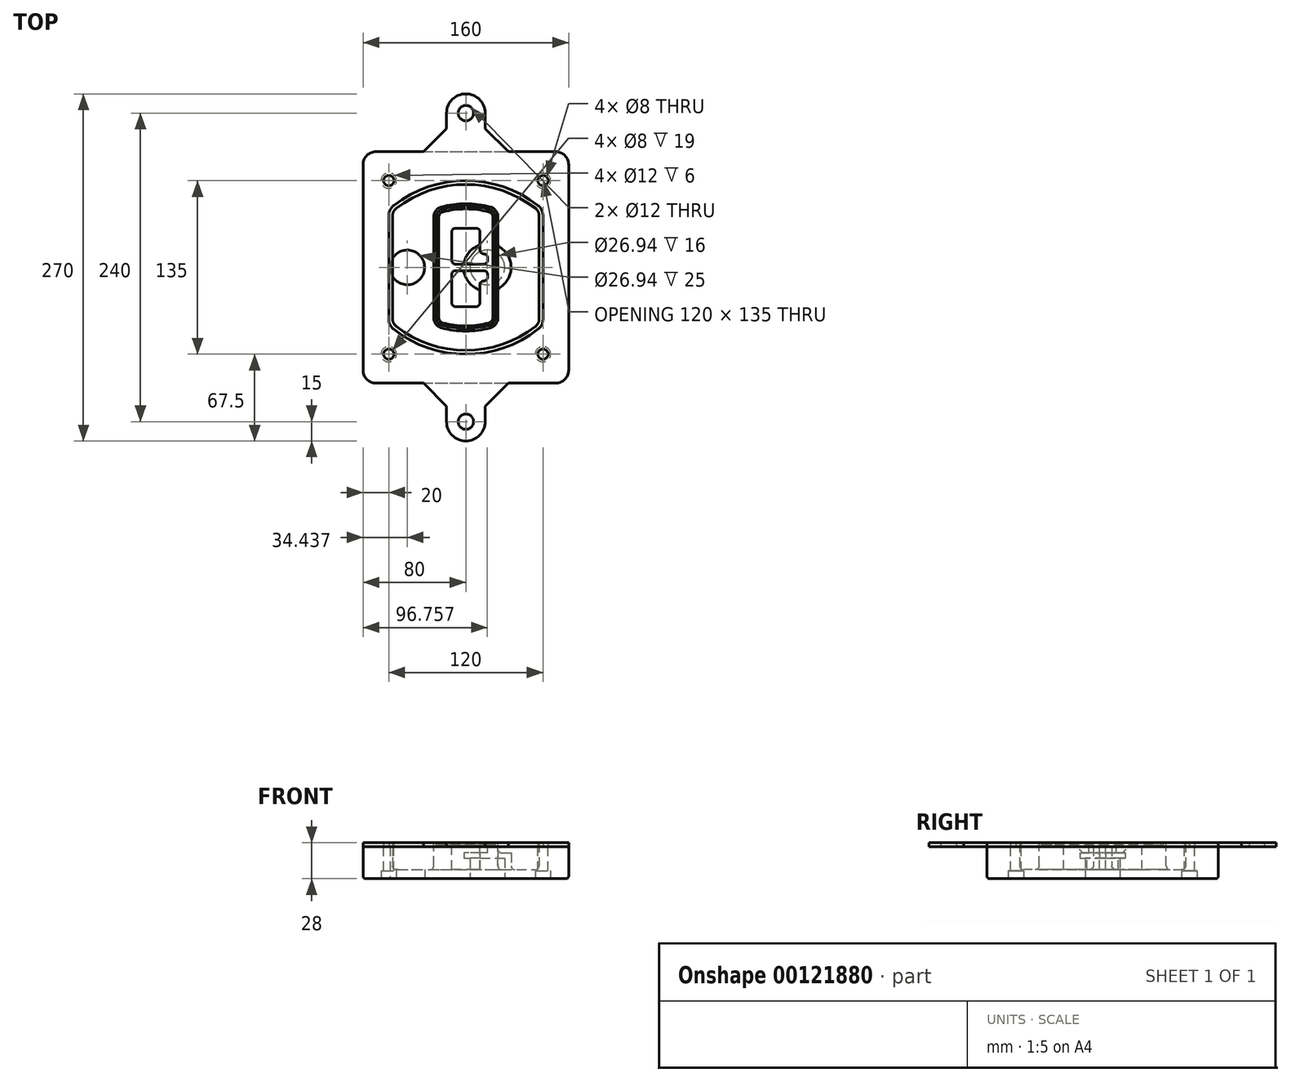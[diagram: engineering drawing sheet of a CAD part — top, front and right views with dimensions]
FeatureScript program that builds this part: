
annotation { "Feature Type Name" : "Feature", "Feature Type Description" : "" }
export const myFeature = defineFeature(function(context is Context, id is Id, definition is map)
    precondition{}
    {
        {
            var Q0;
            Q0=qCreatedBy(makeId("Top.planeOp"),FACE);
            var sketch = newSketch(context, id + "F0", { "sketchPlane" : qUnion([Q0])});
            skPoint(sketch, "E0.rect.middle", {"position": v(0, 0) * mm});
            skLineSegment(sketch, "E1.bottom", {"start": v(-70, -90) * mm, "end": v(70, -90) * mm});
            skLineSegment(sketch, "E1.top", {"start": v(-70, 90) * mm, "end": v(70, 90) * mm});
            skLineSegment(sketch, "E1.left", {"start": v(-80, -80) * mm, "end": v(-80, 80) * mm});
            skLineSegment(sketch, "E1.right", {"start": v(80, -80) * mm, "end": v(80, 80) * mm});
            skLineSegment(sketch, "E2", {"start": v(-80, 90) * mm, "end": v(80, -90) * mm, "construction": true});
            skLineSegment(sketch, "E3", {"start": v(80, 90) * mm, "end": v(-80, -90) * mm, "construction": true});
            skCircle(sketch, "E4", {"center": v(-60, 67.5) * mm, "radius": 4 * mm});
            skCircle(sketch, "E5", {"center": v(60, 67.5) * mm, "radius": 4 * mm});
            skCircle(sketch, "E6", {"center": v(60, -67.5) * mm, "radius": 4 * mm});
            skCircle(sketch, "E7", {"center": v(-60, -67.5) * mm, "radius": 4 * mm});
            skLineSegment(sketch, "E8", {"start": v(-60, 67.5) * mm, "end": v(60, 67.5) * mm, "construction": true});
            skLineSegment(sketch, "E9", {"start": v(60, 67.5) * mm, "end": v(60, -67.5) * mm, "construction": true});
            skLineSegment(sketch, "E10", {"start": v(60, -67.5) * mm, "end": v(-60, -67.5) * mm, "construction": true});
            skLineSegment(sketch, "E11", {"start": v(-60, -67.5) * mm, "end": v(-60, 67.5) * mm, "construction": true});
            skLineSegment(sketch, "E12", {"start": v(-60, 40.3) * mm, "end": v(-60, -40.3) * mm});
            skLineSegment(sketch, "E13", {"start": v(60, 40.3) * mm, "end": v(60, -40.3) * mm});
            skArc(sketch, "E14", {"start": v(56.15, 48.18) * mm, "mid": v(0, 67.5) * mm, "end": v(-56.15, 48.18) * mm});
            skArc(sketch, "E15", {"start": v(-56.15, -48.18) * mm, "mid": v(0, -67.5) * mm, "end": v(56.15, -48.18) * mm});
            skLineSegment(sketch, "E16", {"start": v(-60, 0) * mm, "end": v(60, 0) * mm, "construction": true});
            skPoint(sketch, "E17.visualSharp", {"position": v(-60, -45) * mm});
            skArc(sketch, "E17.filletArc", {"start": v(-60, -40.3) * mm, "mid": v(-58.99, -44.68) * mm, "end": v(-56.15, -48.18) * mm});
            skPoint(sketch, "E18.visualSharp", {"position": v(-60, 45) * mm});
            skArc(sketch, "E18.filletArc", {"start": v(-56.15, 48.18) * mm, "mid": v(-58.99, 44.68) * mm, "end": v(-60, 40.3) * mm});
            skPoint(sketch, "E19.visualSharp", {"position": v(60, 45) * mm});
            skArc(sketch, "E19.filletArc", {"start": v(60, 40.3) * mm, "mid": v(58.99, 44.68) * mm, "end": v(56.15, 48.18) * mm});
            skPoint(sketch, "E20.visualSharp", {"position": v(60, -45) * mm});
            skArc(sketch, "E20.filletArc", {"start": v(56.15, -48.18) * mm, "mid": v(58.99, -44.68) * mm, "end": v(60, -40.3) * mm});
            skPoint(sketch, "E21.visualSharp", {"position": v(-80, 90) * mm});
            skArc(sketch, "E21.filletArc", {"start": v(-70, 90) * mm, "mid": v(-77.07, 87.07) * mm, "end": v(-80, 80) * mm});
            skPoint(sketch, "E22.visualSharp", {"position": v(80, 90) * mm});
            skArc(sketch, "E22.filletArc", {"start": v(80, 80) * mm, "mid": v(77.07, 87.07) * mm, "end": v(70, 90) * mm});
            skPoint(sketch, "E23.visualSharp", {"position": v(80, -90) * mm});
            skArc(sketch, "E23.filletArc", {"start": v(70, -90) * mm, "mid": v(77.07, -87.07) * mm, "end": v(80, -80) * mm});
            skPoint(sketch, "E24.visualSharp", {"position": v(-80, -90) * mm});
            skArc(sketch, "E24.filletArc", {"start": v(-80, -80) * mm, "mid": v(-77.07, -87.07) * mm, "end": v(-70, -90) * mm});
            skArc(sketch, "E25.0", {"start": v(57, 40.3) * mm, "mid": v(56.3, 43.36) * mm, "end": v(54.3, 45.81) * mm});
            skLineSegment(sketch, "E25.1", {"start": v(57, 40.3) * mm, "end": v(57, -40.3) * mm});
            skArc(sketch, "E25.2", {"start": v(54.3, -45.81) * mm, "mid": v(56.3, -43.36) * mm, "end": v(57, -40.3) * mm});
            skArc(sketch, "E25.3", {"start": v(-54.3, -45.81) * mm, "mid": v(0, -64.5) * mm, "end": v(54.3, -45.81) * mm});
            skArc(sketch, "E25.4", {"start": v(-57, -40.3) * mm, "mid": v(-56.3, -43.36) * mm, "end": v(-54.3, -45.81) * mm});
            skArc(sketch, "E25.5", {"start": v(54.3, 45.81) * mm, "mid": v(0, 64.5) * mm, "end": v(-54.3, 45.81) * mm});
            skLineSegment(sketch, "E25.6", {"start": v(-57, 40.3) * mm, "end": v(-57, -40.3) * mm});
            skArc(sketch, "E25.7", {"start": v(-54.3, 45.81) * mm, "mid": v(-56.3, 43.36) * mm, "end": v(-57, 40.3) * mm});
            skArc(sketch, "E26.0", {"start": v(-58.62, 51.33) * mm, "mid": v(-62.58, 46.43) * mm, "end": v(-64, 40.3) * mm});
            skArc(sketch, "E26.1", {"start": v(58.62, 51.33) * mm, "mid": v(0, 71.5) * mm, "end": v(-58.62, 51.33) * mm});
            skArc(sketch, "E26.2", {"start": v(64, 40.3) * mm, "mid": v(62.58, 46.43) * mm, "end": v(58.62, 51.33) * mm});
            skLineSegment(sketch, "E26.3", {"start": v(64, 40.3) * mm, "end": v(64, -40.3) * mm});
            skArc(sketch, "E26.4", {"start": v(58.62, -51.33) * mm, "mid": v(62.58, -46.43) * mm, "end": v(64, -40.3) * mm});
            skLineSegment(sketch, "E26.5", {"start": v(-64, 40.3) * mm, "end": v(-64, -40.3) * mm});
            skArc(sketch, "E26.6", {"start": v(-58.62, -51.33) * mm, "mid": v(0, -71.5) * mm, "end": v(58.62, -51.33) * mm});
            skArc(sketch, "E26.7", {"start": v(-64, -40.3) * mm, "mid": v(-62.58, -46.43) * mm, "end": v(-58.62, -51.33) * mm});
            skSolve(sketch);
        }
        {
            var Q0;
            Q0=makeQuery(id+"F0.imprint","IMPRINT",FACE,{"disambiguationData":[TD([[makeQuery(id+"F0.imprint","IMPRINT",EDGE,{"derivedFrom":sQuery(id+"F0.wireOp",EDGE,"E1.bottom")}),1.0]])]});
            var Q1;
            Q1=makeQuery(id+"F0.imprint","IMPRINT",FACE,{"disambiguationData":[TD([[makeQuery(id+"F0.imprint","IMPRINT",EDGE,{"derivedFrom":sQuery(id+"F0.wireOp",EDGE,"E12")}),1.0]])]});
            var Q2;
            Q2=makeQuery(id+"F0.imprint","IMPRINT",FACE,{"disambiguationData":[TD([[makeQuery(id+"F0.imprint","IMPRINT",EDGE,{"derivedFrom":sQuery(id+"F0.wireOp",EDGE,"E25.0")}),1.0]])]});
            var Q3;
            Q3=makeQuery(id+"F0.imprint","IMPRINT",FACE,{"disambiguationData":[TD([[makeQuery(id+"F0.imprint","IMPRINT",EDGE,{"derivedFrom":sQuery(id+"F0.wireOp",EDGE,"E12")}),-1.0]])]});
            extrude(context, id + "F1", {"entities" : qUnion([Q0, Q1, Q2, Q3]), "oppositeDirection" : true, "depth" : 25 * mm});
        }
        {
            var Q0;
            Q0=makeQuery(id+"F0.imprint","IMPRINT",FACE,{"disambiguationData":[TD([[makeQuery(id+"F0.imprint","IMPRINT",EDGE,{"derivedFrom":sQuery(id+"F0.wireOp",EDGE,"E12")}),1.0]])]});
            extrude(context, id + "F2", {"entities" : qUnion([Q0]), "operationType" : NewBodyOperationType.ADD, "depth" : 3 * mm});
        }
        {
            var Q0;
            Q0=makeQuery(id+"F0.imprint","IMPRINT",FACE,{"disambiguationData":[TD([[makeQuery(id+"F0.imprint","IMPRINT",EDGE,{"derivedFrom":sQuery(id+"F0.wireOp",EDGE,"E25.0")}),1.0]])]});
            extrude(context, id + "F3", {"entities" : qUnion([Q0]), "operationType" : NewBodyOperationType.REMOVE, "oppositeDirection" : true, "depth" : 18 * mm});
        }
        {
            var Q0;
            Q0=makeQuery(id+"F2.opExtrude","CAP_FACE",FACE,{"disambiguationData":[OSD([sQuery(id+"F0.wireOp",EDGE,"E12"),sQuery(id+"F0.wireOp",EDGE,"E13"),sQuery(id+"F0.wireOp",EDGE,"E14"),sQuery(id+"F0.wireOp",EDGE,"E15"),sQuery(id+"F0.wireOp",EDGE,"E17.filletArc"),sQuery(id+"F0.wireOp",EDGE,"E18.filletArc"),sQuery(id+"F0.wireOp",EDGE,"E19.filletArc"),sQuery(id+"F0.wireOp",EDGE,"E20.filletArc"),sQuery(id+"F0.wireOp",EDGE,"E25.0"),sQuery(id+"F0.wireOp",EDGE,"E25.1"),sQuery(id+"F0.wireOp",EDGE,"E25.2"),sQuery(id+"F0.wireOp",EDGE,"E25.3"),sQuery(id+"F0.wireOp",EDGE,"E25.4"),sQuery(id+"F0.wireOp",EDGE,"E25.5"),sQuery(id+"F0.wireOp",EDGE,"E25.6"),sQuery(id+"F0.wireOp",EDGE,"E25.7")])],"isStart":false});
            var sketch = newSketch(context, id + "F4", { "sketchPlane" : qUnion([Q0])});
            skArc(sketch, "E27.0", {"start": v(-19.08, -46.97) * mm, "mid": v(0, -49.5) * mm, "end": v(19.08, -46.97) * mm});
            skArc(sketch, "E28.0", {"start": v(19.08, 46.97) * mm, "mid": v(0, 49.5) * mm, "end": v(-19.08, 46.97) * mm});
            skLineSegment(sketch, "E29", {"start": v(-25, 39.25) * mm, "end": v(-25, -39.25) * mm});
            skLineSegment(sketch, "E30", {"start": v(25, 39.25) * mm, "end": v(25, -39.25) * mm});
            skLineSegment(sketch, "E31", {"start": v(-25, 45.1) * mm, "end": v(25, 45.1) * mm, "construction": true});
            skLineSegment(sketch, "E32", {"start": v(-25, -45.1) * mm, "end": v(25, -45.1) * mm, "construction": true});
            skPoint(sketch, "E33.visualSharp", {"position": v(-25, 45.1) * mm});
            skArc(sketch, "E33.filletArc", {"start": v(-19.08, 46.97) * mm, "mid": v(-23.35, 44.11) * mm, "end": v(-25, 39.25) * mm});
            skPoint(sketch, "E34.visualSharp", {"position": v(25, 45.1) * mm});
            skArc(sketch, "E34.filletArc", {"start": v(25, 39.25) * mm, "mid": v(23.35, 44.11) * mm, "end": v(19.08, 46.97) * mm});
            skPoint(sketch, "E35.visualSharp", {"position": v(25, -45.1) * mm});
            skArc(sketch, "E35.filletArc", {"start": v(19.08, -46.97) * mm, "mid": v(23.35, -44.11) * mm, "end": v(25, -39.25) * mm});
            skPoint(sketch, "E36.visualSharp", {"position": v(-25, -45.1) * mm});
            skArc(sketch, "E36.filletArc", {"start": v(-25, -39.25) * mm, "mid": v(-23.35, -44.11) * mm, "end": v(-19.08, -46.97) * mm});
            skArc(sketch, "E37.0", {"start": v(54.3, 45.81) * mm, "mid": v(0, 64.5) * mm, "end": v(-54.3, 45.81) * mm});
            skArc(sketch, "E37.1", {"start": v(-54.3, 45.81) * mm, "mid": v(-56.3, 43.36) * mm, "end": v(-57, 40.3) * mm});
            skLineSegment(sketch, "E37.2", {"start": v(-57, 40.3) * mm, "end": v(-57, -40.3) * mm});
            skArc(sketch, "E37.3", {"start": v(-57, -40.3) * mm, "mid": v(-56.3, -43.36) * mm, "end": v(-54.3, -45.81) * mm});
            skArc(sketch, "E37.4", {"start": v(-54.3, -45.81) * mm, "mid": v(0, -64.5) * mm, "end": v(54.3, -45.81) * mm});
            skArc(sketch, "E37.5", {"start": v(54.3, -45.81) * mm, "mid": v(56.3, -43.36) * mm, "end": v(57, -40.3) * mm});
            skLineSegment(sketch, "E37.6", {"start": v(57, 40.3) * mm, "end": v(57, -40.3) * mm});
            skArc(sketch, "E37.7", {"start": v(57, 40.3) * mm, "mid": v(56.3, 43.36) * mm, "end": v(54.3, 45.81) * mm});
            skLineSegment(sketch, "E38.0", {"start": v(23, 39.25) * mm, "end": v(23, -39.25) * mm});
            skArc(sketch, "E38.1", {"start": v(18.56, -45.04) * mm, "mid": v(21.76, -42.9) * mm, "end": v(23, -39.25) * mm});
            skArc(sketch, "E38.2", {"start": v(-18.56, -45.04) * mm, "mid": v(0, -47.5) * mm, "end": v(18.56, -45.04) * mm});
            skArc(sketch, "E38.3", {"start": v(-23, -39.25) * mm, "mid": v(-21.76, -42.9) * mm, "end": v(-18.56, -45.04) * mm});
            skLineSegment(sketch, "E38.4", {"start": v(-23, 39.25) * mm, "end": v(-23, -39.25) * mm});
            skArc(sketch, "E38.5", {"start": v(23, 39.25) * mm, "mid": v(21.76, 42.9) * mm, "end": v(18.56, 45.04) * mm});
            skArc(sketch, "E38.6", {"start": v(-18.56, 45.04) * mm, "mid": v(-21.76, 42.9) * mm, "end": v(-23, 39.25) * mm});
            skArc(sketch, "E38.7", {"start": v(18.56, 45.04) * mm, "mid": v(0, 47.5) * mm, "end": v(-18.56, 45.04) * mm});
            skArc(sketch, "E39.0", {"start": v(21, 39.25) * mm, "mid": v(20.18, 41.68) * mm, "end": v(18.04, 43.1) * mm});
            skLineSegment(sketch, "E39.1", {"start": v(21, 39.25) * mm, "end": v(21, -39.25) * mm});
            skArc(sketch, "E39.2", {"start": v(18.04, -43.1) * mm, "mid": v(20.18, -41.68) * mm, "end": v(21, -39.25) * mm});
            skArc(sketch, "E39.3", {"start": v(-18.04, -43.1) * mm, "mid": v(0, -45.5) * mm, "end": v(18.04, -43.1) * mm});
            skArc(sketch, "E39.4", {"start": v(-21, -39.25) * mm, "mid": v(-20.18, -41.68) * mm, "end": v(-18.04, -43.1) * mm});
            skArc(sketch, "E39.5", {"start": v(18.04, 43.1) * mm, "mid": v(0, 45.5) * mm, "end": v(-18.04, 43.1) * mm});
            skLineSegment(sketch, "E39.6", {"start": v(-21, 39.25) * mm, "end": v(-21, -39.25) * mm});
            skArc(sketch, "E39.7", {"start": v(-18.04, 43.1) * mm, "mid": v(-20.18, 41.68) * mm, "end": v(-21, 39.25) * mm});
            skLineSegment(sketch, "E40", {"start": v(-25, 0) * mm, "end": v(25, 0) * mm, "construction": true});
            skLineSegment(sketch, "E41", {"start": v(-11, 5.5) * mm, "end": v(-11, 27.5) * mm});
            skLineSegment(sketch, "E42", {"start": v(-8, 30.5) * mm, "end": v(8, 30.5) * mm});
            skLineSegment(sketch, "E43", {"start": v(11, 27.5) * mm, "end": v(11, 13.5) * mm});
            skLineSegment(sketch, "E44", {"start": v(14, 10.5) * mm, "end": v(14, 10.5) * mm});
            skLineSegment(sketch, "E45", {"start": v(17, 7.5) * mm, "end": v(17, 5.5) * mm});
            skLineSegment(sketch, "E46", {"start": v(14, 2.5) * mm, "end": v(-8, 2.5) * mm});
            skPoint(sketch, "E47.visualSharp", {"position": v(-11, 30.5) * mm});
            skArc(sketch, "E47.filletArc", {"start": v(-8, 30.5) * mm, "mid": v(-10.12, 29.62) * mm, "end": v(-11, 27.5) * mm});
            skPoint(sketch, "E48.visualSharp", {"position": v(11, 30.5) * mm});
            skArc(sketch, "E48.filletArc", {"start": v(11, 27.5) * mm, "mid": v(10.12, 29.62) * mm, "end": v(8, 30.5) * mm});
            skPoint(sketch, "E49.visualSharp", {"position": v(11, 10.5) * mm});
            skArc(sketch, "E49.filletArc", {"start": v(11, 13.5) * mm, "mid": v(11.88, 11.38) * mm, "end": v(14, 10.5) * mm});
            skPoint(sketch, "E50.visualSharp", {"position": v(17, 10.5) * mm});
            skArc(sketch, "E50.filletArc", {"start": v(17, 7.5) * mm, "mid": v(16.12, 9.62) * mm, "end": v(14, 10.5) * mm});
            skPoint(sketch, "E51.visualSharp", {"position": v(17, 2.5) * mm});
            skArc(sketch, "E51.filletArc", {"start": v(14, 2.5) * mm, "mid": v(16.12, 3.38) * mm, "end": v(17, 5.5) * mm});
            skPoint(sketch, "E52.visualSharp", {"position": v(-11, 2.5) * mm});
            skArc(sketch, "E52.filletArc", {"start": v(-11, 5.5) * mm, "mid": v(-10.12, 3.38) * mm, "end": v(-8, 2.5) * mm});
            skLineSegment(sketch, "E53.0.MirrorCS", {"start": v(14, -2.5) * mm, "end": v(-8, -2.5) * mm});
            skArc(sketch, "E54.0.MirrorCS", {"start": v(-11, -5.5) * mm, "mid": v(-10.12, -3.38) * mm, "end": v(-8, -2.5) * mm});
            skLineSegment(sketch, "E55.0.MirrorCS", {"start": v(-11, -5.5) * mm, "end": v(-11, -27.5) * mm});
            skArc(sketch, "E56.0.MirrorCS", {"start": v(-8, -30.5) * mm, "mid": v(-10.12, -29.62) * mm, "end": v(-11, -27.5) * mm});
            skLineSegment(sketch, "E57.0.MirrorCS", {"start": v(-8, -30.5) * mm, "end": v(8, -30.5) * mm});
            skArc(sketch, "E58.0.MirrorCS", {"start": v(11, -27.5) * mm, "mid": v(10.12, -29.62) * mm, "end": v(8, -30.5) * mm});
            skLineSegment(sketch, "E59.0.MirrorCS", {"start": v(11, -27.5) * mm, "end": v(11, -13.5) * mm});
            skArc(sketch, "E60.0.MirrorCS", {"start": v(11, -13.5) * mm, "mid": v(11.88, -11.38) * mm, "end": v(14, -10.5) * mm});
            skArc(sketch, "E61.0.MirrorCS", {"start": v(17, -7.5) * mm, "mid": v(16.12, -9.62) * mm, "end": v(14, -10.5) * mm});
            skLineSegment(sketch, "E62.0.MirrorCS", {"start": v(17, -7.5) * mm, "end": v(17, -5.5) * mm});
            skArc(sketch, "E63.0.MirrorCS", {"start": v(14, -2.5) * mm, "mid": v(16.12, -3.38) * mm, "end": v(17, -5.5) * mm});
            skSolve(sketch);
        }
        {
            var Q0;
            Q0=makeQuery(id+"F4.imprint","IMPRINT",FACE,{"disambiguationData":[TD([[makeQuery(id+"F4.imprint","IMPRINT",EDGE,{"derivedFrom":sQuery(id+"F4.wireOp",EDGE,"E27.0")}),1.0]])]});
            var Q1;
            Q1=makeQuery(id+"F4.imprint","IMPRINT",FACE,{"disambiguationData":[TD([[makeQuery(id+"F4.imprint","IMPRINT",EDGE,{"derivedFrom":sQuery(id+"F4.wireOp",EDGE,"E38.0")}),-1.0]])]});
            var Q2;
            Q2=makeQuery(id+"F4.imprint","IMPRINT",FACE,{"disambiguationData":[TD([[makeQuery(id+"F4.imprint","IMPRINT",EDGE,{"derivedFrom":sQuery(id+"F4.wireOp",EDGE,"E39.0")}),1.0]])]});
            extrude(context, id + "F5", {"entities" : qUnion([Q0, Q1, Q2]), "operationType" : NewBodyOperationType.ADD, "endBound" : BoundingType.UP_TO_NEXT, "oppositeDirection" : true, "depth" : 25 * mm});
        }
        {
            var Q0;
            Q0=makeQuery(id+"F4.imprint","IMPRINT",FACE,{"disambiguationData":[TD([[makeQuery(id+"F4.imprint","IMPRINT",EDGE,{"derivedFrom":sQuery(id+"F4.wireOp",EDGE,"E38.0")}),-1.0]])]});
            extrude(context, id + "F6", {"entities" : qUnion([Q0]), "operationType" : NewBodyOperationType.REMOVE, "oppositeDirection" : true, "depth" : 2 * mm});
        }
        {
            var Q0;
            Q0=makeQuery(id+"F1.opExtrude","CAP_FACE",FACE,{"disambiguationData":[OSD([sQuery(id+"F0.wireOp",EDGE,"E1.bottom"),sQuery(id+"F0.wireOp",EDGE,"E1.top"),sQuery(id+"F0.wireOp",EDGE,"E1.left"),sQuery(id+"F0.wireOp",EDGE,"E1.right"),sQuery(id+"F0.wireOp",EDGE,"E4"),sQuery(id+"F0.wireOp",EDGE,"E5"),sQuery(id+"F0.wireOp",EDGE,"E6"),sQuery(id+"F0.wireOp",EDGE,"E7"),sQuery(id+"F0.wireOp",EDGE,"E21.filletArc"),sQuery(id+"F0.wireOp",EDGE,"E22.filletArc"),sQuery(id+"F0.wireOp",EDGE,"E23.filletArc"),sQuery(id+"F0.wireOp",EDGE,"E24.filletArc")])],"isStart":false});
            var sketch = newSketch(context, id + "F7", { "sketchPlane" : qUnion([Q0])});
            skCircle(sketch, "E64", {"center": v(16.76, 0) * mm, "radius": 13.47 * mm});
            skCircle(sketch, "E65", {"center": v(-45.56, 0) * mm, "radius": 13.47 * mm});
            skLineSegment(sketch, "E66", {"start": v(80, 0) * mm, "end": v(-80, 0) * mm});
            skCircle(sketch, "E67", {"center": v(16.76, 0) * mm, "radius": 18.47 * mm});
            skCircle(sketch, "E68", {"center": v(60, -67.5) * mm, "radius": 6 * mm});
            skCircle(sketch, "E69", {"center": v(-60, -67.5) * mm, "radius": 6 * mm});
            skCircle(sketch, "E70", {"center": v(-60, 67.5) * mm, "radius": 6 * mm});
            skCircle(sketch, "E71", {"center": v(60, 67.5) * mm, "radius": 6 * mm});
            skSolve(sketch);
        }
        {
            var Q0;
            {var subQ1=sQuery(id+"F7.wireOp",EDGE,"E66");var subQ4=sQuery(id+"F7.wireOp",EDGE,"E64");var subQ6=makeQuery(id+"F7.imprint","INTERSECT",VERTEX,{"disambiguationData":[OD(0.0)],"derivedFrom":[subQ4,subQ1]});Q0=makeQuery(id+"F7.imprint","IMPRINT",FACE,{"disambiguationData":[TD([[makeQuery(id+"F7.imprint","IMPRINT",EDGE,{"disambiguationData":[TD([[subQ6,-1.0]])],"derivedFrom":subQ4}),-1.0]])]});}
            var Q1;
            {var subQ0=sQuery(id+"F7.wireOp",EDGE,"E66");var subQ1=sQuery(id+"F7.wireOp",EDGE,"E64");var subQ3=makeQuery(id+"F7.imprint","INTERSECT",VERTEX,{"disambiguationData":[OD(0.0)],"derivedFrom":[subQ1,subQ0]});Q1=makeQuery(id+"F7.imprint","IMPRINT",FACE,{"disambiguationData":[TD([[makeQuery(id+"F7.imprint","IMPRINT",EDGE,{"disambiguationData":[TD([[subQ3,-1.0]])],"derivedFrom":subQ1}),1.0]])]});}
            var Q2;
            {var subQ0=sQuery(id+"F7.wireOp",EDGE,"E66");var subQ1=sQuery(id+"F7.wireOp",EDGE,"E64");var subQ3=makeQuery(id+"F7.imprint","INTERSECT",VERTEX,{"disambiguationData":[OD(0.0)],"derivedFrom":[subQ1,subQ0]});Q2=makeQuery(id+"F7.imprint","IMPRINT",FACE,{"disambiguationData":[TD([[makeQuery(id+"F7.imprint","IMPRINT",EDGE,{"disambiguationData":[TD([[subQ3,1.0]])],"derivedFrom":subQ1}),1.0]])]});}
            var Q3;
            {var subQ1=sQuery(id+"F7.wireOp",EDGE,"E66");var subQ4=sQuery(id+"F7.wireOp",EDGE,"E64");var subQ6=makeQuery(id+"F7.imprint","INTERSECT",VERTEX,{"disambiguationData":[OD(0.0)],"derivedFrom":[subQ4,subQ1]});Q3=makeQuery(id+"F7.imprint","IMPRINT",FACE,{"disambiguationData":[TD([[makeQuery(id+"F7.imprint","IMPRINT",EDGE,{"disambiguationData":[TD([[subQ6,1.0]])],"derivedFrom":subQ4}),-1.0]])]});}
            extrude(context, id + "F8", {"entities" : qUnion([Q0, Q1, Q2, Q3]), "operationType" : NewBodyOperationType.ADD, "oppositeDirection" : true, "depth" : 20 * mm});
        }
        {
            var Q0;
            {var subQ0=sQuery(id+"F7.wireOp",EDGE,"E66");var subQ1=sQuery(id+"F7.wireOp",EDGE,"E64");var subQ3=makeQuery(id+"F7.imprint","INTERSECT",VERTEX,{"disambiguationData":[OD(0.0)],"derivedFrom":[subQ1,subQ0]});Q0=makeQuery(id+"F7.imprint","IMPRINT",FACE,{"disambiguationData":[TD([[makeQuery(id+"F7.imprint","IMPRINT",EDGE,{"disambiguationData":[TD([[subQ3,-1.0]])],"derivedFrom":subQ1}),1.0]])]});}
            var Q1;
            {var subQ0=sQuery(id+"F7.wireOp",EDGE,"E66");var subQ1=sQuery(id+"F7.wireOp",EDGE,"E64");var subQ3=makeQuery(id+"F7.imprint","INTERSECT",VERTEX,{"disambiguationData":[OD(0.0)],"derivedFrom":[subQ1,subQ0]});Q1=makeQuery(id+"F7.imprint","IMPRINT",FACE,{"disambiguationData":[TD([[makeQuery(id+"F7.imprint","IMPRINT",EDGE,{"disambiguationData":[TD([[subQ3,1.0]])],"derivedFrom":subQ1}),1.0]])]});}
            extrude(context, id + "F9", {"entities" : qUnion([Q0, Q1]), "operationType" : NewBodyOperationType.REMOVE, "oppositeDirection" : true, "depth" : 16 * mm});
        }
        {
            var Q0;
            {var subQ0=sQuery(id+"F7.wireOp",EDGE,"E66");var subQ1=sQuery(id+"F7.wireOp",EDGE,"E65");var subQ3=makeQuery(id+"F7.imprint","INTERSECT",VERTEX,{"disambiguationData":[OD(0.0)],"derivedFrom":[subQ1,subQ0]});Q0=makeQuery(id+"F7.imprint","IMPRINT",FACE,{"disambiguationData":[TD([[makeQuery(id+"F7.imprint","IMPRINT",EDGE,{"disambiguationData":[TD([[subQ3,-1.0]])],"derivedFrom":subQ1}),1.0]])]});}
            var Q1;
            {var subQ0=sQuery(id+"F7.wireOp",EDGE,"E66");var subQ1=sQuery(id+"F7.wireOp",EDGE,"E65");var subQ3=makeQuery(id+"F7.imprint","INTERSECT",VERTEX,{"disambiguationData":[OD(0.0)],"derivedFrom":[subQ1,subQ0]});Q1=makeQuery(id+"F7.imprint","IMPRINT",FACE,{"disambiguationData":[TD([[makeQuery(id+"F7.imprint","IMPRINT",EDGE,{"disambiguationData":[TD([[subQ3,1.0]])],"derivedFrom":subQ1}),1.0]])]});}
            extrude(context, id + "F10", {"entities" : qUnion([Q0, Q1]), "operationType" : NewBodyOperationType.REMOVE, "oppositeDirection" : true, "depth" : 25 * mm});
        }
        {
            var Q0;
            Q0=makeQuery(id+"F7.imprint","IMPRINT",FACE,{"disambiguationData":[TD([[makeQuery(id+"F7.imprint","IMPRINT",EDGE,{"derivedFrom":sQuery(id+"F7.wireOp",EDGE,"E68")}),1.0]])]});
            var Q1;
            Q1=makeQuery(id+"F7.imprint","IMPRINT",FACE,{"disambiguationData":[TD([[makeQuery(id+"F7.imprint","IMPRINT",EDGE,{"derivedFrom":makeQuery(id+"F1.opExtrude","CAP_EDGE",EDGE,{"disambiguationData":[OSD([sQuery(id+"F0.wireOp",EDGE,"E5")])],"isStart":false})}),-1.0]])]});
            var Q2;
            Q2=makeQuery(id+"F7.imprint","IMPRINT",FACE,{"disambiguationData":[TD([[makeQuery(id+"F7.imprint","IMPRINT",EDGE,{"derivedFrom":sQuery(id+"F7.wireOp",EDGE,"E69")}),1.0]])]});
            var Q3;
            Q3=makeQuery(id+"F7.imprint","IMPRINT",FACE,{"disambiguationData":[TD([[makeQuery(id+"F7.imprint","IMPRINT",EDGE,{"derivedFrom":makeQuery(id+"F1.opExtrude","CAP_EDGE",EDGE,{"disambiguationData":[OSD([sQuery(id+"F0.wireOp",EDGE,"E4")])],"isStart":false})}),-1.0]])]});
            var Q4;
            Q4=makeQuery(id+"F7.imprint","IMPRINT",FACE,{"disambiguationData":[TD([[makeQuery(id+"F7.imprint","IMPRINT",EDGE,{"derivedFrom":sQuery(id+"F7.wireOp",EDGE,"E70")}),1.0]])]});
            var Q5;
            Q5=makeQuery(id+"F7.imprint","IMPRINT",FACE,{"disambiguationData":[TD([[makeQuery(id+"F7.imprint","IMPRINT",EDGE,{"derivedFrom":makeQuery(id+"F1.opExtrude","CAP_EDGE",EDGE,{"disambiguationData":[OSD([sQuery(id+"F0.wireOp",EDGE,"E7")])],"isStart":false})}),-1.0]])]});
            var Q6;
            Q6=makeQuery(id+"F7.imprint","IMPRINT",FACE,{"disambiguationData":[TD([[makeQuery(id+"F7.imprint","IMPRINT",EDGE,{"derivedFrom":sQuery(id+"F7.wireOp",EDGE,"E71")}),1.0]])]});
            var Q7;
            Q7=makeQuery(id+"F7.imprint","IMPRINT",FACE,{"disambiguationData":[TD([[makeQuery(id+"F7.imprint","IMPRINT",EDGE,{"derivedFrom":makeQuery(id+"F1.opExtrude","CAP_EDGE",EDGE,{"disambiguationData":[OSD([sQuery(id+"F0.wireOp",EDGE,"E6")])],"isStart":false})}),-1.0]])]});
            extrude(context, id + "F11", {"entities" : qUnion([Q0, Q1, Q2, Q3, Q4, Q5, Q6, Q7]), "operationType" : NewBodyOperationType.REMOVE, "oppositeDirection" : true, "depth" : 6 * mm});
        }
        {
            var Q0;
            Q0=makeQuery(id+"F9.boolean.opBoolean","COPY",FACE,{"derivedFrom":makeQuery(id+"F9.opExtrude","CAP_FACE",FACE,{"disambiguationData":[OSD([sQuery(id+"F7.wireOp",EDGE,"E64")])],"isStart":false})});
            var sketch = newSketch(context, id + "F12", { "sketchPlane" : qUnion([Q0])});
            skArc(sketch, "E72.0", {"start": v(11, 17.55) * mm, "mid": v(2.57, 11.82) * mm, "end": v(-1.54, 2.5) * mm});
            skArc(sketch, "E72.1", {"start": v(-1.54, -2.5) * mm, "mid": v(2.57, -11.82) * mm, "end": v(11, -17.55) * mm});
            skLineSegment(sketch, "E73", {"start": v(-1.54, -2.5) * mm, "end": v(14, -2.5) * mm});
            skLineSegment(sketch, "E74.0", {"start": v(14, 2.5) * mm, "end": v(-1.54, 2.5) * mm});
            skArc(sketch, "E74.1", {"start": v(14, 2.5) * mm, "mid": v(16.12, 3.38) * mm, "end": v(17, 5.5) * mm});
            skLineSegment(sketch, "E74.2", {"start": v(17, 7.5) * mm, "end": v(17, 5.5) * mm});
            skArc(sketch, "E74.3", {"start": v(17, 7.5) * mm, "mid": v(16.12, 9.62) * mm, "end": v(14, 10.5) * mm});
            skArc(sketch, "E74.4", {"start": v(11, 13.5) * mm, "mid": v(11.88, 11.38) * mm, "end": v(14, 10.5) * mm});
            skLineSegment(sketch, "E74.5", {"start": v(11, 17.55) * mm, "end": v(11, 13.5) * mm});
            skLineSegment(sketch, "E74.7", {"start": v(14, -2.5) * mm, "end": v(-1.54, -2.5) * mm});
            skArc(sketch, "E74.8", {"start": v(14, -2.5) * mm, "mid": v(16.12, -3.38) * mm, "end": v(17, -5.5) * mm});
            skLineSegment(sketch, "E74.9", {"start": v(17, -7.5) * mm, "end": v(17, -5.5) * mm});
            skArc(sketch, "E74.10", {"start": v(17, -7.5) * mm, "mid": v(16.12, -9.62) * mm, "end": v(14, -10.5) * mm});
            skArc(sketch, "E74.11", {"start": v(11, -13.5) * mm, "mid": v(11.88, -11.38) * mm, "end": v(14, -10.5) * mm});
            skLineSegment(sketch, "E74.12", {"start": v(11, -17.55) * mm, "end": v(11, -13.5) * mm});
            skPoint(sketch, "E75.orphan", {"position": v(11, -27.5) * mm});
            skPoint(sketch, "E76.orphan", {"position": v(-8, -2.5) * mm});
            skPoint(sketch, "E77.orphan", {"position": v(-8, 2.5) * mm});
            skPoint(sketch, "E78.orphan", {"position": v(11, 27.5) * mm});
            skSolve(sketch);
        }
        {
            var Q0;
            {var subQ7=sQuery(id+"F12.wireOp",EDGE,"E72.0");var subQ14=sQuery(id+"F12.wireOp",EDGE,"E72.1");var subQ16=sQuery(id+"F12.wireOp",EDGE,"E74.1");var subQ18=sQuery(id+"F12.wireOp",EDGE,"E74.8");Q0=qUnion([makeQuery(id+"F12.imprint","IMPRINT",FACE,{"disambiguationData":[TD([[makeQuery(id+"F12.imprint","IMPRINT",EDGE,{"derivedFrom":subQ7}),1.0]])]}),makeQuery(id+"F12.imprint","IMPRINT",FACE,{"disambiguationData":[TD([[makeQuery(id+"F12.imprint","IMPRINT",EDGE,{"derivedFrom":subQ14}),1.0]])]}),makeQuery(id+"F12.imprint","IMPRINT",FACE,{"disambiguationData":[TD([[makeQuery(id+"F12.imprint","IMPRINT",EDGE,{"derivedFrom":subQ16}),1.0]])]}),makeQuery(id+"F12.imprint","IMPRINT",FACE,{"disambiguationData":[TD([[makeQuery(id+"F12.imprint","IMPRINT",EDGE,{"derivedFrom":subQ18}),-1.0]])]})]);}
            var Q1;
            Q1=makeQuery(id+"F5.boolean.opBoolean","SPLIT",FACE,{"disambiguationData":[TD([makeQuery(id+"F5.opExtrude","SWEPT_FACE",FACE,{"disambiguationData":[OSD([sQuery(id+"F4.wireOp",EDGE,"E41")])]})])],"derivedFrom":makeQuery(id+"F3.boolean.opBoolean","COPY",FACE,{"derivedFrom":makeQuery(id+"F3.opExtrude","CAP_FACE",FACE,{"disambiguationData":[OSD([sQuery(id+"F0.wireOp",EDGE,"E25.0"),sQuery(id+"F0.wireOp",EDGE,"E25.1"),sQuery(id+"F0.wireOp",EDGE,"E25.2"),sQuery(id+"F0.wireOp",EDGE,"E25.3"),sQuery(id+"F0.wireOp",EDGE,"E25.4"),sQuery(id+"F0.wireOp",EDGE,"E25.5"),sQuery(id+"F0.wireOp",EDGE,"E25.6"),sQuery(id+"F0.wireOp",EDGE,"E25.7")])],"isStart":false})})});
            extrude(context, id + "F13", {"entities" : qUnion([Q0]), "operationType" : NewBodyOperationType.REMOVE, "endBound" : BoundingType.UP_TO_SURFACE, "endBoundEntityFace" : qUnion([Q1]), "depth" : 25 * mm});
        }
        {
            var Q0;
            Q0=makeQuery(id+"F3.boolean.opBoolean","COPY",EDGE,{"derivedFrom":makeQuery(id+"F3.opExtrude","CAP_EDGE",EDGE,{"disambiguationData":[OSD([sQuery(id+"F0.wireOp",EDGE,"E25.6")])],"isStart":false})});
            var Q1;
            Q1=makeQuery(id+"F8.boolean.opBoolean","INTERSECT",EDGE,{"derivedFrom":[makeQuery(id+"F5.opExtrude","SWEPT_FACE",FACE,{"disambiguationData":[OSD([sQuery(id+"F4.wireOp",EDGE,"E30")])]}),makeQuery(id+"F8.opExtrude","CAP_FACE",FACE,{"disambiguationData":[OSD([sQuery(id+"F7.wireOp",EDGE,"E67")])],"isStart":false})]});
            var Q2;
            Q2=makeQuery(id+"F8.boolean.opBoolean","INTERSECT",EDGE,{"disambiguationData":[OD(1.0)],"derivedFrom":[makeQuery(id+"F5.opExtrude","SWEPT_FACE",FACE,{"disambiguationData":[OSD([sQuery(id+"F4.wireOp",EDGE,"E30")])]}),makeQuery(id+"F8.opExtrude","SWEPT_FACE",FACE,{"disambiguationData":[OSD([sQuery(id+"F7.wireOp",EDGE,"E67")])]})]});
            var Q3;
            {var subQ0=sQuery(id+"F4.wireOp",EDGE,"E30");Q3=makeQuery(id+"F8.boolean.opBoolean","SPLIT",EDGE,{"disambiguationData":[TD([makeQuery(id+"F5.opExtrude","SWEPT_FACE",FACE,{"disambiguationData":[OSD([sQuery(id+"F4.wireOp",EDGE,"E35.filletArc")])]})])],"derivedFrom":makeQuery(id+"F5.opExtrude","CAP_EDGE",EDGE,{"disambiguationData":[OSD([subQ0])],"isStart":false})});}
            var Q4;
            {var subQ0=sQuery(id+"F0.wireOp",EDGE,"E25.7");var subQ1=sQuery(id+"F0.wireOp",EDGE,"E25.1");var subQ2=sQuery(id+"F0.wireOp",EDGE,"E25.6");var subQ3=sQuery(id+"F0.wireOp",EDGE,"E25.5");var subQ4=sQuery(id+"F0.wireOp",EDGE,"E25.4");var subQ5=sQuery(id+"F0.wireOp",EDGE,"E25.0");var subQ6=sQuery(id+"F0.wireOp",EDGE,"E25.2");var subQ7=sQuery(id+"F0.wireOp",EDGE,"E25.3");Q4=makeQuery(id+"F8.boolean.opBoolean","INTERSECT",EDGE,{"derivedFrom":[makeQuery(id+"F5.boolean.opBoolean","SPLIT",FACE,{"disambiguationData":[TD([makeQuery(id+"F2.opExtrude","SWEPT_FACE",FACE,{"disambiguationData":[OSD([subQ5])]})])],"derivedFrom":makeQuery(id+"F3.boolean.opBoolean","COPY",FACE,{"derivedFrom":makeQuery(id+"F3.opExtrude","CAP_FACE",FACE,{"disambiguationData":[OSD([subQ5,subQ1,subQ6,subQ7,subQ4,subQ3,subQ2,subQ0])],"isStart":false})})}),makeQuery(id+"F8.opExtrude","SWEPT_FACE",FACE,{"disambiguationData":[OSD([sQuery(id+"F7.wireOp",EDGE,"E67")])]})]});}
            var Q5;
            Q5=makeQuery(id+"F8.boolean.opBoolean","INTERSECT",EDGE,{"disambiguationData":[OD(0.0)],"derivedFrom":[makeQuery(id+"F5.opExtrude","SWEPT_FACE",FACE,{"disambiguationData":[OSD([sQuery(id+"F4.wireOp",EDGE,"E30")])]}),makeQuery(id+"F8.opExtrude","SWEPT_FACE",FACE,{"disambiguationData":[OSD([sQuery(id+"F7.wireOp",EDGE,"E67")])]})]});
            fillet(context, id + "F14", {"entities" : qUnion([Q0, Q1, Q2, Q3, Q4, Q5]), "radius" : 3 * mm, "tangentPropagation" : true, "allowEdgeOverflow" : false});
        }
        {
            var Q0;
            Q0=makeQuery(id+"F1.opExtrude","CAP_EDGE",EDGE,{"disambiguationData":[OSD([sQuery(id+"F0.wireOp",EDGE,"E1.bottom")])],"isStart":false});
            fillet(context, id + "F15", {"entities" : qUnion([Q0]), "radius" : 2 * mm, "tangentPropagation" : true, "allowEdgeOverflow" : false});
        }
        {
            var Q0;
            {var subQ0=sQuery(id+"F0.wireOp",EDGE,"E22.filletArc");var subQ1=sQuery(id+"F0.wireOp",EDGE,"E7");var subQ2=sQuery(id+"F0.wireOp",EDGE,"E6");var subQ3=sQuery(id+"F0.wireOp",EDGE,"E5");var subQ4=sQuery(id+"F0.wireOp",EDGE,"E4");var subQ5=sQuery(id+"F0.wireOp",EDGE,"E1.bottom");var subQ6=sQuery(id+"F0.wireOp",EDGE,"E21.filletArc");var subQ7=sQuery(id+"F0.wireOp",EDGE,"E1.top");var subQ8=sQuery(id+"F0.wireOp",EDGE,"E1.left");var subQ9=sQuery(id+"F0.wireOp",EDGE,"E1.right");var subQ10=sQuery(id+"F0.wireOp",EDGE,"E23.filletArc");var subQ11=sQuery(id+"F0.wireOp",EDGE,"E24.filletArc");Q0=makeQuery(id+"F2.boolean.opBoolean","SPLIT",FACE,{"disambiguationData":[TD([makeQuery(id+"F1.opExtrude","SWEPT_FACE",FACE,{"disambiguationData":[OSD([subQ5])]})])],"derivedFrom":makeQuery(id+"F1.opExtrude","CAP_FACE",FACE,{"disambiguationData":[OSD([subQ5,subQ7,subQ8,subQ9,subQ4,subQ3,subQ2,subQ1,subQ6,subQ0,subQ10,subQ11])],"isStart":true})});}
            var sketch = newSketch(context, id + "F16", { "sketchPlane" : qUnion([Q0])});
            skLineSegment(sketch, "E79.0", {"start": v(80, -80) * mm, "end": v(80, 80) * mm});
            skArc(sketch, "E80.0", {"start": v(80, 80) * mm, "mid": v(77.07, 87.07) * mm, "end": v(70, 90) * mm});
            skLineSegment(sketch, "E81.0", {"start": v(-70, 90) * mm, "end": v(70, 90) * mm});
            skArc(sketch, "E82.0", {"start": v(-70, 90) * mm, "mid": v(-77.07, 87.07) * mm, "end": v(-80, 80) * mm});
            skLineSegment(sketch, "E83.0", {"start": v(-80, -80) * mm, "end": v(-80, 80) * mm});
            skArc(sketch, "E84.0", {"start": v(-80, -80) * mm, "mid": v(-77.07, -87.07) * mm, "end": v(-70, -90) * mm});
            skLineSegment(sketch, "E85.0", {"start": v(-70, -90) * mm, "end": v(70, -90) * mm});
            skArc(sketch, "E86.0", {"start": v(70, -90) * mm, "mid": v(77.07, -87.07) * mm, "end": v(80, -80) * mm});
            skCircle(sketch, "E87.0", {"center": v(60, -67.5) * mm, "radius": 4 * mm});
            skCircle(sketch, "E88.0", {"center": v(60, 67.5) * mm, "radius": 4 * mm});
            skCircle(sketch, "E89.0", {"center": v(-60, 67.5) * mm, "radius": 4 * mm});
            skLineSegment(sketch, "E90.0.5", {"start": v(70, 90) * mm, "end": v(-70, 90) * mm});
            skLineSegment(sketch, "E90.0.7", {"start": v(-80, 80) * mm, "end": v(-80, -80) * mm});
            skCircle(sketch, "E91.0", {"center": v(-60, -67.5) * mm, "radius": 4 * mm});
            skArc(sketch, "E92.0", {"start": v(-56.15, -48.18) * mm, "mid": v(0, -67.5) * mm, "end": v(56.15, -48.18) * mm});
            skArc(sketch, "E93.0", {"start": v(56.15, -48.18) * mm, "mid": v(58.99, -44.68) * mm, "end": v(60, -40.3) * mm});
            skLineSegment(sketch, "E94.0", {"start": v(60, 40.3) * mm, "end": v(60, -40.3) * mm});
            skArc(sketch, "E95.0", {"start": v(60, 40.3) * mm, "mid": v(58.99, 44.68) * mm, "end": v(56.15, 48.18) * mm});
            skArc(sketch, "E96.0", {"start": v(56.15, 48.18) * mm, "mid": v(0, 67.5) * mm, "end": v(-56.15, 48.18) * mm});
            skArc(sketch, "E97.0", {"start": v(-56.15, 48.18) * mm, "mid": v(-58.99, 44.68) * mm, "end": v(-60, 40.3) * mm});
            skLineSegment(sketch, "E98.0", {"start": v(-60, 40.3) * mm, "end": v(-60, -40.3) * mm});
            skArc(sketch, "E99.0", {"start": v(-60, -40.3) * mm, "mid": v(-58.99, -44.68) * mm, "end": v(-56.15, -48.18) * mm});
            skLineSegment(sketch, "E100", {"start": v(0, 90) * mm, "end": v(0, 120) * mm, "construction": true});
            skPoint(sketch, "E100.endSnap0", {"position": v(0, 90) * mm});
            skCircle(sketch, "E101", {"center": v(0, 120) * mm, "radius": 6 * mm});
            skArc(sketch, "E102", {"start": v(15, 120) * mm, "mid": v(0, 135) * mm, "end": v(-15, 120) * mm});
            skLineSegment(sketch, "E103", {"start": v(-15, 120) * mm, "end": v(-15, 108) * mm});
            skLineSegment(sketch, "E104", {"start": v(-15, 108) * mm, "end": v(-33, 90) * mm});
            skLineSegment(sketch, "E105", {"start": v(15, 120) * mm, "end": v(15, 108) * mm});
            skLineSegment(sketch, "E106", {"start": v(15, 108) * mm, "end": v(33, 90) * mm});
            skLineSegment(sketch, "E107", {"start": v(-80, 0) * mm, "end": v(80, 0) * mm, "construction": true});
            skArc(sketch, "E108.MirrorCS", {"start": v(-15, 120) * mm, "mid": v(0, 135) * mm, "end": v(15, 120) * mm});
            skLineSegment(sketch, "E109.MirrorCS", {"start": v(15, -108) * mm, "end": v(33, -90) * mm});
            skCircle(sketch, "E110.MirrorC", {"center": v(0, -120) * mm, "radius": 6 * mm});
            skLineSegment(sketch, "E111.MirrorCS", {"start": v(15, -120) * mm, "end": v(15, -108) * mm});
            skArc(sketch, "E112.MirrorCS", {"start": v(15, -120) * mm, "mid": v(0, -135) * mm, "end": v(-15, -120) * mm});
            skLineSegment(sketch, "E113.MirrorCS", {"start": v(-15, -108) * mm, "end": v(-33, -90) * mm});
            skLineSegment(sketch, "E114.MirrorCS", {"start": v(-15, -120) * mm, "end": v(-15, -108) * mm});
            skPoint(sketch, "E115.MirrorP", {"position": v(0, -90) * mm});
            skArc(sketch, "E116.MirrorCS", {"start": v(-15, -120) * mm, "mid": v(0, -135) * mm, "end": v(15, -120) * mm});
            skLineSegment(sketch, "E117.MirrorCS", {"start": v(0, -90) * mm, "end": v(0, -120) * mm, "construction": true});
            skSolve(sketch);
        }
        {
            var Q0;
            Q0=makeQuery(id+"F16.imprint","IMPRINT",FACE,{"disambiguationData":[TD([[makeQuery(id+"F16.imprint","IMPRINT",EDGE,{"derivedFrom":sQuery(id+"F16.wireOp",EDGE,"E105")}),-1.0]])]});
            var Q1;
            Q1=makeQuery(id+"F16.imprint","IMPRINT",FACE,{"disambiguationData":[TD([[makeQuery(id+"F16.imprint","IMPRINT",EDGE,{"derivedFrom":sQuery(id+"F16.wireOp",EDGE,"E87.0")}),-1.0]])]});
            var Q2;
            Q2=makeQuery(id+"F16.imprint","IMPRINT",FACE,{"disambiguationData":[TD([[makeQuery(id+"F16.imprint","IMPRINT",EDGE,{"derivedFrom":sQuery(id+"F16.wireOp",EDGE,"E111.MirrorCS")}),1.0]])]});
            var Q3;
            Q3=makeQuery(id+"F2.opExtrude","CAP_FACE",FACE,{"disambiguationData":[OSD([sQuery(id+"F0.wireOp",EDGE,"E12"),sQuery(id+"F0.wireOp",EDGE,"E13"),sQuery(id+"F0.wireOp",EDGE,"E14"),sQuery(id+"F0.wireOp",EDGE,"E15"),sQuery(id+"F0.wireOp",EDGE,"E17.filletArc"),sQuery(id+"F0.wireOp",EDGE,"E18.filletArc"),sQuery(id+"F0.wireOp",EDGE,"E19.filletArc"),sQuery(id+"F0.wireOp",EDGE,"E20.filletArc"),sQuery(id+"F0.wireOp",EDGE,"E25.0"),sQuery(id+"F0.wireOp",EDGE,"E25.1"),sQuery(id+"F0.wireOp",EDGE,"E25.2"),sQuery(id+"F0.wireOp",EDGE,"E25.3"),sQuery(id+"F0.wireOp",EDGE,"E25.4"),sQuery(id+"F0.wireOp",EDGE,"E25.5"),sQuery(id+"F0.wireOp",EDGE,"E25.6"),sQuery(id+"F0.wireOp",EDGE,"E25.7")])],"isStart":false});
            extrude(context, id + "F17", {"entities" : qUnion([Q0, Q1, Q2]), "endBound" : BoundingType.UP_TO_SURFACE, "endBoundEntityFace" : qUnion([Q3]), "depth" : 25 * mm});
        }
    });
